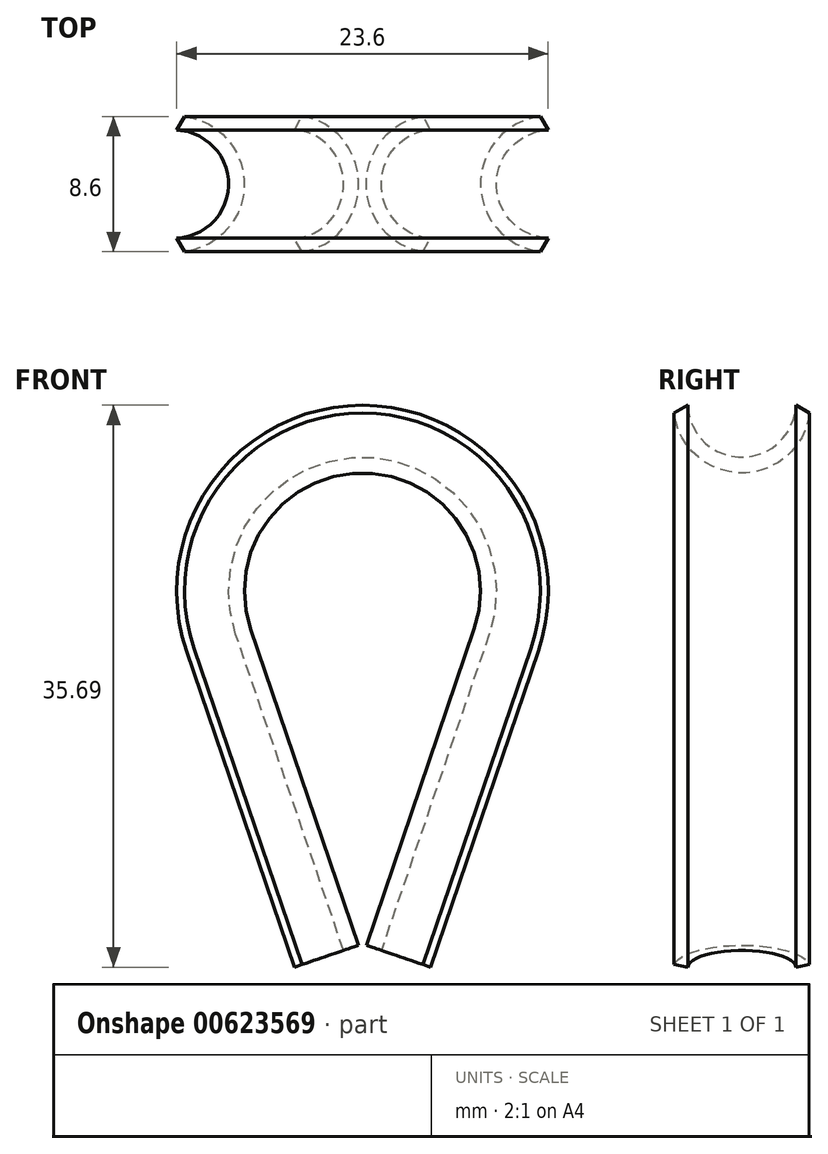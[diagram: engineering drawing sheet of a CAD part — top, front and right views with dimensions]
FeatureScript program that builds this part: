
annotation { "Feature Type Name" : "Feature", "Feature Type Description" : "" }
export const myFeature = defineFeature(function(context is Context, id is Id, definition is map)
    precondition{}
    {
        {
            var Q0;
            Q0=qCreatedBy(makeId("Front.planeOp"),FACE);
            var sketch = newSketch(context, id + "F0", { "sketchPlane" : qUnion([Q0])});
            skArc(sketch, "E0", {"start": v(7.1, 20.08) * mm, "mid": v(0, 30) * mm, "end": v(-7.1, 20.08) * mm});
            skLineSegment(sketch, "E1", {"start": v(-7.1, 20.08) * mm, "end": v(-0.25, 0) * mm});
            skLineSegment(sketch, "E2", {"start": v(0.25, 0) * mm, "end": v(7.1, 20.08) * mm});
            skLineSegment(sketch, "E3", {"start": v(-0.25, 0) * mm, "end": v(0.25, 0) * mm, "construction": true});
            skSolve(sketch);
        }
        {
            var Q0;
            Q0=qCreatedBy(makeId("Right.planeOp"),FACE);
            var sketch = newSketch(context, id + "F1", { "sketchPlane" : qUnion([Q0])});
            skArc(sketch, "E4", {"start": v(4.3, 33.8) * mm, "mid": v(0, 30) * mm, "end": v(-4.3, 33.8) * mm});
            skLineSegment(sketch, "E5", {"start": v(-4.3, 33.8) * mm, "end": v(4.3, 33.8) * mm, "construction": true});
            skArc(sketch, "E6", {"start": v(3.43, 34.3) * mm, "mid": v(0, 31) * mm, "end": v(-3.43, 34.3) * mm});
            skLineSegment(sketch, "E7", {"start": v(-4.3, 33.8) * mm, "end": v(-3.43, 34.3) * mm});
            skLineSegment(sketch, "E8", {"start": v(3.43, 34.3) * mm, "end": v(4.3, 33.8) * mm});
            skLineSegment(sketch, "E9", {"start": v(0, 31) * mm, "end": v(0, 30) * mm, "construction": true});
            skSolve(sketch);
        }
        {
            var Q0;
            Q0 = qSketchRegion(id + "F1", true);
            var Q1;
            Q1=sQuery(id+"F0.wireOp",EDGE,"E0");
            var Q2;
            Q2=sQuery(id+"F0.wireOp",EDGE,"E2");
            var Q3;
            Q3=sQuery(id+"F0.wireOp",EDGE,"E1");
            sweep(context, id + "F2", {"profiles" : qUnion([Q0]), "path" : qUnion([Q1, Q2, Q3])});
        }
    });
